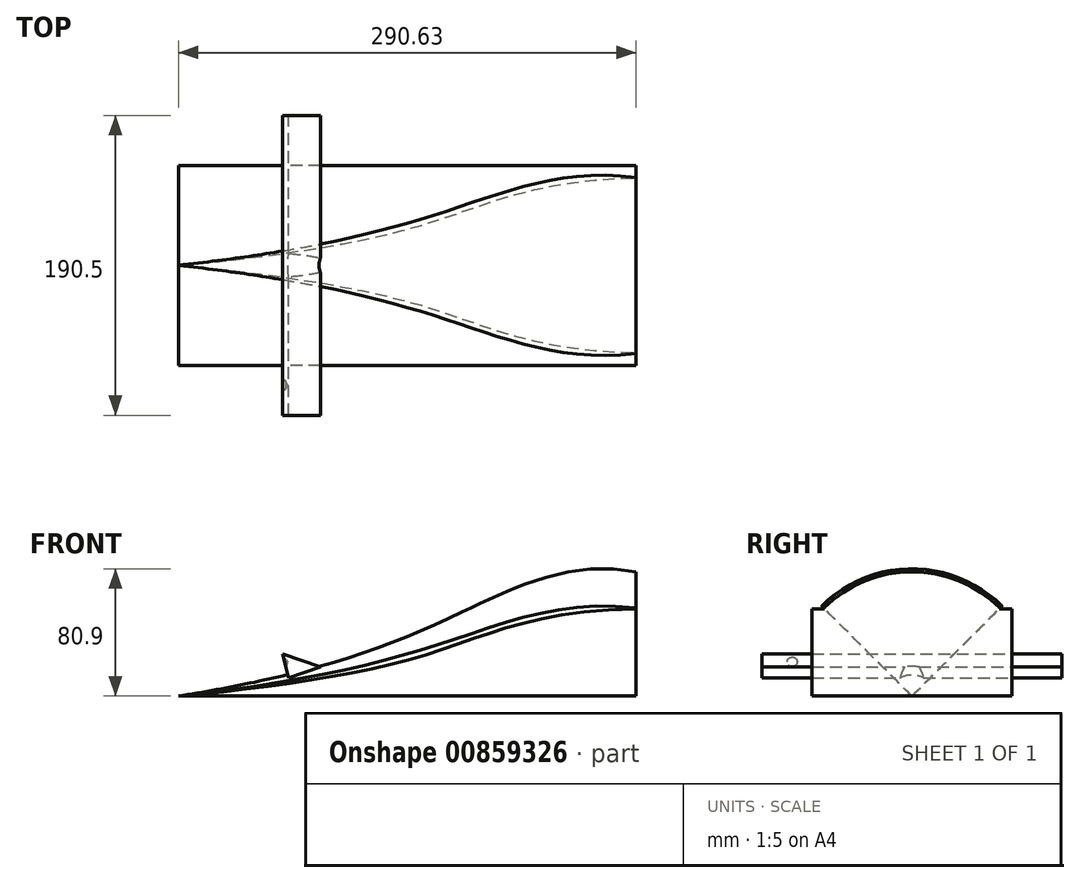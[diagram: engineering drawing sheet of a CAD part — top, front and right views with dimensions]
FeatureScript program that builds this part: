
annotation { "Feature Type Name" : "Feature", "Feature Type Description" : "" }
export const myFeature = defineFeature(function(context is Context, id is Id, definition is map)
    precondition{}
    {
        {
            var Q0;
            Q0=qCreatedBy(makeId("Front.planeOp"),FACE);
            var sketch = newSketch(context, id + "F0", { "sketchPlane" : qUnion([Q0])});
            skLineSegment(sketch, "E0", {"start": v(-156.2, 0) * mm, "end": v(134.42, 0) * mm});
            skLineSegment(sketch, "E1", {"start": v(134.42, 0) * mm, "end": v(134.42, 79.02) * mm});
            skFitSpline(sketch, "E2", {"points": [v(-156.2, 0) * mm, v(13.23, 48.3) * mm, v(134.42, 79.02) * mm], "startDerivative": vector(421.15, 66.6) * mm, "endDerivative": vector(304.8, -55.84) * mm});
            skSolve(sketch);
        }
        {
            var Q0;
            Q0=makeQuery(id+"F0.imprint","IMPRINT",FACE,{"disambiguationData":[TD([[makeQuery(id+"F0.imprint","IMPRINT",EDGE,{"derivedFrom":sQuery(id+"F0.wireOp",EDGE,"E0")}),1.0]])]});
            var Q1;
            Q1=sQuery(id+"F0.wireOp",EDGE,"E0");
            revolve(context, id + "F1", {"surfaceOperationType" : NewSurfaceOperationType.NEW, "entities" : qUnion([Q0]), "axis" : qUnion([Q1]), "revolveType" : RevolveType.SYMMETRIC, "angle" : 90 * degree});
        }
        {
            var Q0;
            Q0=qCreatedBy(makeId("Front.planeOp"),FACE);
            var sketch = newSketch(context, id + "F2", { "sketchPlane" : qUnion([Q0])});
            skLineSegment(sketch, "E3", {"start": v(-65.94, 18.53) * mm, "end": v(-90.04, 26.7) * mm});
            skLineSegment(sketch, "E4", {"start": v(-90.04, 26.7) * mm, "end": v(-86.16, 11.59) * mm});
            skLineSegment(sketch, "E5", {"start": v(-86.16, 11.59) * mm, "end": v(-65.94, 18.53) * mm});
            skSolve(sketch);
        }
        {
            var Q0;
            Q0=makeQuery(id+"F2.imprint","IMPRINT",FACE,{"disambiguationData":[TD([[makeQuery(id+"F2.imprint","IMPRINT",EDGE,{"derivedFrom":sQuery(id+"F2.wireOp",EDGE,"E3")}),1.0]])]});
            extrude(context, id + "F3", {"entities" : qUnion([Q0]), "operationType" : NewBodyOperationType.ADD, "endBound" : BoundingType.SYMMETRIC, "depth" : 190.5 * mm, "offsetDistance" : 25.4 * mm});
        }
        {
            var Q0;
            Q0=makeQuery(id+"F3.opExtrude","SWEPT_FACE",FACE,{"disambiguationData":[OSD([sQuery(id+"F2.wireOp",EDGE,"E4")])]});
            var sketch = newSketch(context, id + "F4", { "sketchPlane" : qUnion([Q0])});
            skCircle(sketch, "E6", {"center": v(76, 43.1) * mm, "radius": 2.66 * mm});
            skSolve(sketch);
        }
        {
            var Q0;
            Q0=sQuery(id+"F4.wireOp",VERTEX,"E6.center");
            var Q1;
            Q1=makeQuery(id+"F1.opRevolve","SWEPT_BODY",BODY,{"disambiguationData":[OSD([sQuery(id+"F0.wireOp",EDGE,"E0"),sQuery(id+"F0.wireOp",EDGE,"E1"),sQuery(id+"F0.wireOp",EDGE,"E2")])]});
            hole(context, id + "F5", {"style" : HoleStyle.SIMPLE, "endStyle" : HoleEndStyle.BLIND, "holeDiameter" : 6.35 * mm, "majorDiameter" : 6.35 * mm, "holeDepth" : 0.03 * mm, "isTappedThrough" : true, "tappedDepth" : 12.7 * mm, "tapClearance" : 3, "locations" : qUnion([Q0]), "scope" : qUnion([Q1])});
        }
        {
            var Q0;
            Q0=qCreatedBy(makeId("Front.planeOp"),FACE);
            var sketch = newSketch(context, id + "F6", { "sketchPlane" : qUnion([Q0])});
            skLineSegment(sketch, "E7", {"start": v(0, -22.23) * mm, "end": v(134.42, -22.23) * mm});
            skLineSegment(sketch, "E8", {"start": v(134.42, 0) * mm, "end": v(-156.2, 0) * mm});
            skLineSegment(sketch, "E9", {"start": v(134.42, 0) * mm, "end": v(134.42, 55.54) * mm});
            skFitSpline(sketch, "E10", {"points": [v(134.42, 55.54) * mm, v(0, 26) * mm, v(-156.2, 0) * mm], "startDerivative": vector(-422.5, -10.02) * mm, "endDerivative": vector(-332.13, -29.62) * mm});
            skSolve(sketch);
        }
        {
            var Q0;
            Q0=makeQuery(id+"F6.imprint","IMPRINT",FACE,{"disambiguationData":[TD([[makeQuery(id+"F6.imprint","IMPRINT",EDGE,{"derivedFrom":sQuery(id+"F6.wireOp",EDGE,"E8")}),-1.0]])]});
            extrude(context, id + "F7", {"entities" : qUnion([Q0]), "operationType" : NewBodyOperationType.ADD, "endBound" : BoundingType.SYMMETRIC, "depth" : 127 * mm, "offsetDistance" : 25.4 * mm});
        }
    });
